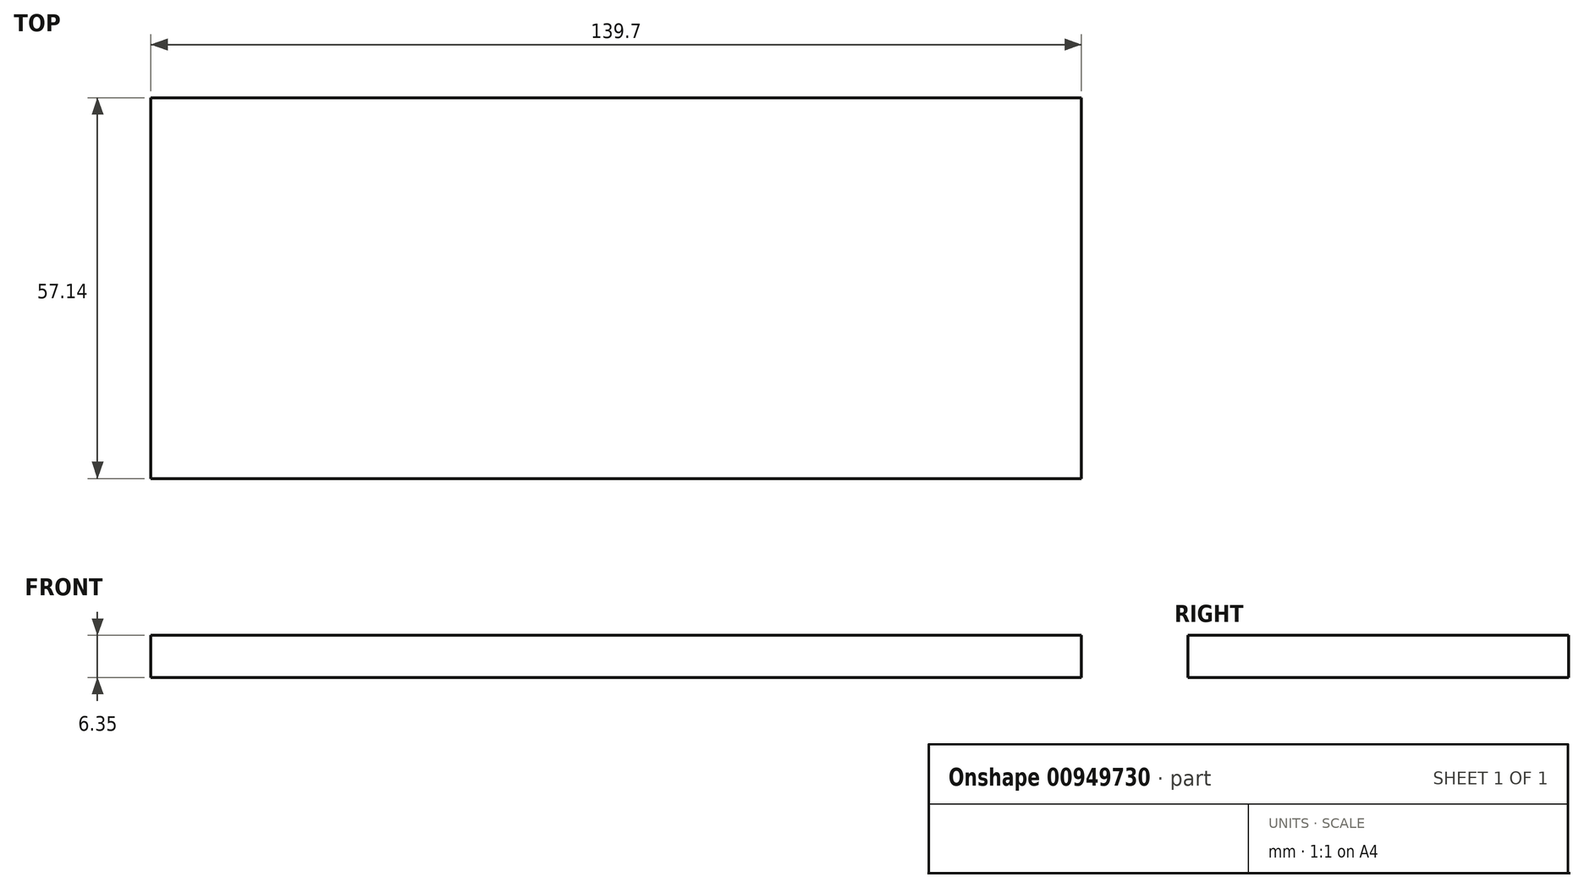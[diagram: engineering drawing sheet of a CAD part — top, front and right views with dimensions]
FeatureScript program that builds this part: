
annotation { "Feature Type Name" : "Feature", "Feature Type Description" : "" }
export const myFeature = defineFeature(function(context is Context, id is Id, definition is map)
    precondition{}
    {
        {
            var Q0;
            Q0=qCreatedBy(makeId("Top.planeOp"),FACE);
            var sketch = newSketch(context, id + "F0", { "sketchPlane" : qUnion([Q0])});
            skLineSegment(sketch, "E0.bottom", {"start": v(-69.85, -28.57) * mm, "end": v(69.85, -28.57) * mm});
            skLineSegment(sketch, "E0.top", {"start": v(-69.85, 28.58) * mm, "end": v(69.85, 28.58) * mm});
            skLineSegment(sketch, "E0.left", {"start": v(-69.85, -28.57) * mm, "end": v(-69.85, 28.58) * mm});
            skLineSegment(sketch, "E0.right", {"start": v(69.85, -28.57) * mm, "end": v(69.85, 28.58) * mm});
            skPoint(sketch, "E0.middle", {"position": v(0, 0) * mm});
            skSolve(sketch);
        }
        {
            var Q0;
            Q0=qSketchRegion(id+"F0",true);
            extrude(context, id + "F1", {"entities" : qUnion([Q0]), "depth" : 6.35 * mm, "offsetDistance" : 25.4 * mm});
        }
    });
